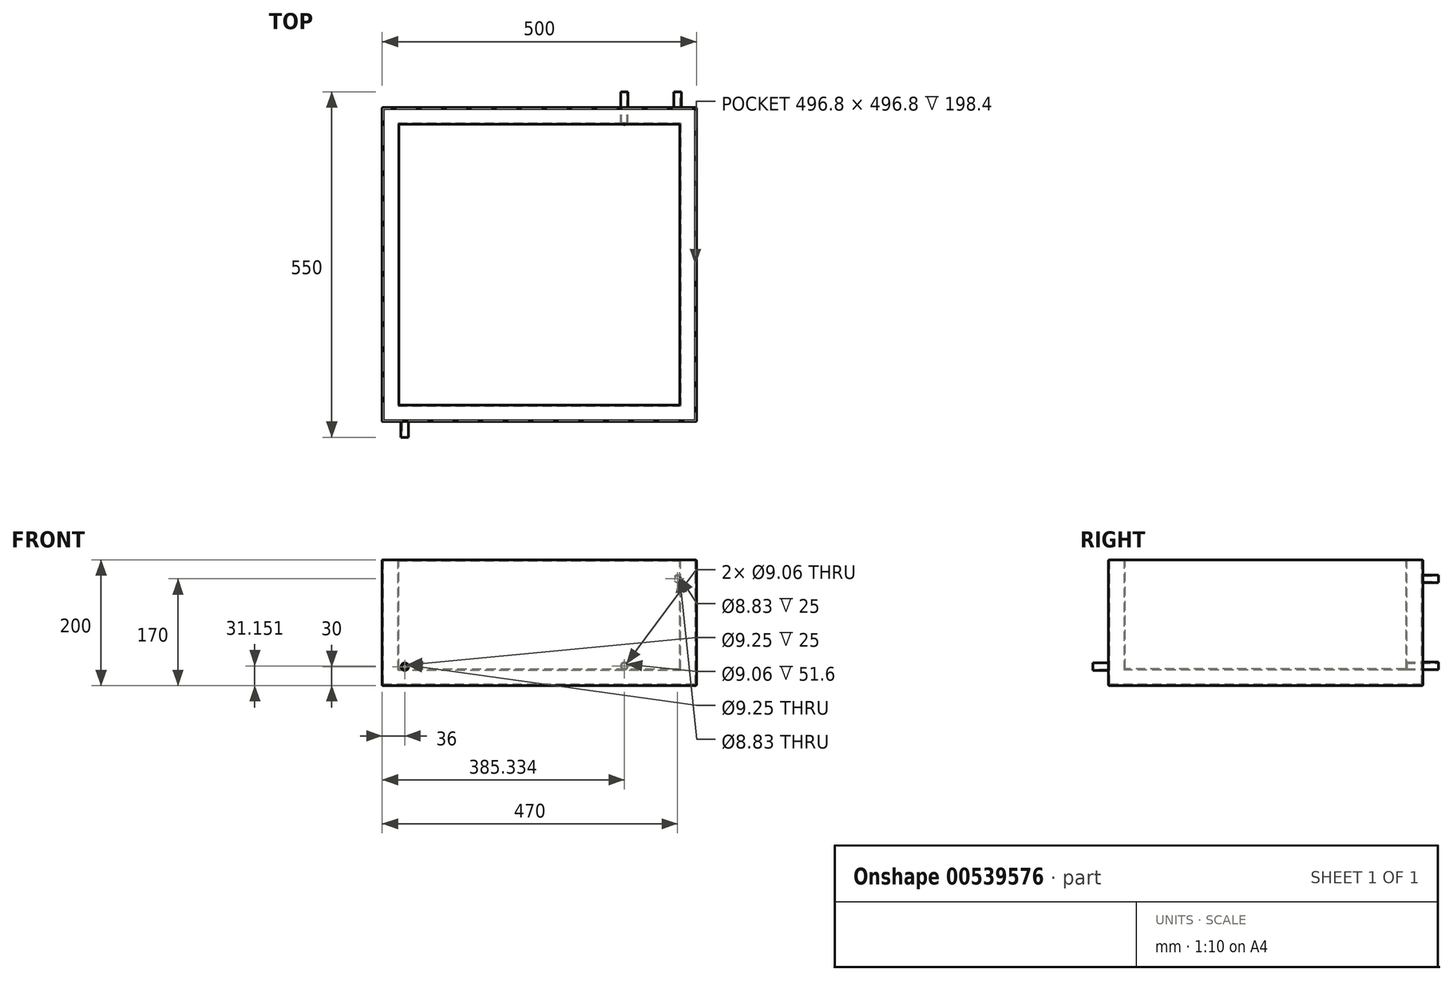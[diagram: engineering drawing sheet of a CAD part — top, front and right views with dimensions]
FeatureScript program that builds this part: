
annotation { "Feature Type Name" : "Feature", "Feature Type Description" : "" }
export const myFeature = defineFeature(function(context is Context, id is Id, definition is map)
    precondition{}
    {
        {
            var Q0;
            Q0=qCreatedBy(makeId("Top.planeOp"),FACE);
            var sketch = newSketch(context, id + "F0", { "sketchPlane" : qUnion([Q0])});
            skLineSegment(sketch, "E0.bottom", {"start": v(250, 250) * mm, "end": v(-250, 250) * mm});
            skLineSegment(sketch, "E0.top", {"start": v(250, -250) * mm, "end": v(-250, -250) * mm});
            skLineSegment(sketch, "E0.left", {"start": v(250, 250) * mm, "end": v(250, -250) * mm});
            skLineSegment(sketch, "E0.right", {"start": v(-250, 250) * mm, "end": v(-250, -250) * mm});
            skPoint(sketch, "E0.middle", {"position": v(0, 0) * mm});
            skSolve(sketch);
        }
        {
            var Q0;
            Q0 = qSketchRegion(id + "F0", true);
            extrude(context, id + "F1", {"entities" : qUnion([Q0]), "depth" : 200 * mm, "offsetDistance" : 25 * mm});
        }
        {
            var Q0;
            Q0=makeQuery(id+"F1.opExtrude","CAP_FACE",FACE,{"disambiguationData":[OSD([sQuery(id+"F0.wireOp",EDGE,"E0.bottom"),sQuery(id+"F0.wireOp",EDGE,"E0.top"),sQuery(id+"F0.wireOp",EDGE,"E0.left"),sQuery(id+"F0.wireOp",EDGE,"E0.right")])],"isStart":true});
            var Q1;
            Q1=makeQuery(id+"F1.opExtrude","SWEPT_EDGE",EDGE,{"disambiguationData":[OSD([sQuery(id+"F0.wireOp",EDGE,"E0.top"),sQuery(id+"F0.wireOp",EDGE,"E0.left")])]});
            var Q2;
            Q2=makeQuery(id+"F1.opExtrude","SWEPT_EDGE",EDGE,{"disambiguationData":[OSD([sQuery(id+"F0.wireOp",EDGE,"E0.top"),sQuery(id+"F0.wireOp",EDGE,"E0.right")])]});
            var Q3;
            Q3=makeQuery(id+"F1.opExtrude","SWEPT_EDGE",EDGE,{"disambiguationData":[OSD([sQuery(id+"F0.wireOp",EDGE,"E0.bottom"),sQuery(id+"F0.wireOp",EDGE,"E0.right")])]});
            var Q4;
            Q4=makeQuery(id+"F1.opExtrude","SWEPT_EDGE",EDGE,{"disambiguationData":[OSD([sQuery(id+"F0.wireOp",EDGE,"E0.bottom"),sQuery(id+"F0.wireOp",EDGE,"E0.left")])]});
            fillet(context, id + "F2", {"entities" : qUnion([Q0, Q1, Q2, Q3, Q4]), "radius" : 1 * mm, "tangentPropagation" : true, "allowEdgeOverflow" : false});
        }
        {
            var Q0;
            Q0=makeQuery(id+"F1.opExtrude","CAP_FACE",FACE,{"disambiguationData":[OSD([sQuery(id+"F0.wireOp",EDGE,"E0.bottom"),sQuery(id+"F0.wireOp",EDGE,"E0.top"),sQuery(id+"F0.wireOp",EDGE,"E0.left"),sQuery(id+"F0.wireOp",EDGE,"E0.right")])],"isStart":false});
            shell(context, id + "F3", {"entities" : qUnion([Q0]), "thickness" : 1.6 * mm});
        }
        {
            var Q0;
            Q0=makeQuery(id+"F1.opExtrude","CAP_FACE",FACE,{"disambiguationData":[OSD([sQuery(id+"F0.wireOp",EDGE,"E0.bottom"),sQuery(id+"F0.wireOp",EDGE,"E0.top"),sQuery(id+"F0.wireOp",EDGE,"E0.left"),sQuery(id+"F0.wireOp",EDGE,"E0.right")])],"isStart":false});
            var sketch = newSketch(context, id + "F4", { "sketchPlane" : qUnion([Q0])});
            skLineSegment(sketch, "E1.bottom", {"start": v(-225, 225) * mm, "end": v(225, 225) * mm});
            skLineSegment(sketch, "E1.top", {"start": v(-225, -225) * mm, "end": v(225, -225) * mm});
            skLineSegment(sketch, "E1.left", {"start": v(-225, 225) * mm, "end": v(-225, -225) * mm});
            skLineSegment(sketch, "E1.right", {"start": v(225, 225) * mm, "end": v(225, -225) * mm});
            skPoint(sketch, "E1.middle", {"position": v(0, 0) * mm});
            skLineSegment(sketch, "E2.bottom", {"start": v(-249, 249) * mm, "end": v(249, 249) * mm});
            skLineSegment(sketch, "E2.top", {"start": v(-249, -249) * mm, "end": v(249, -249) * mm});
            skLineSegment(sketch, "E2.left", {"start": v(-249, 249) * mm, "end": v(-249, -249) * mm});
            skLineSegment(sketch, "E2.right", {"start": v(249, 249) * mm, "end": v(249, -249) * mm});
            skSolve(sketch);
        }
        {
            var Q0;
            Q0=makeQuery(id+"F4.imprint","IMPRINT",FACE,{"disambiguationData":[TD([[makeQuery(id+"F4.imprint","IMPRINT",EDGE,{"derivedFrom":sQuery(id+"F4.wireOp",EDGE,"E1.bottom")}),1.0]])]});
            extrude(context, id + "F5", {"entities" : qUnion([Q0]), "oppositeDirection" : true, "depth" : 1.6 * mm, "offsetDistance" : 25 * mm});
        }
        {
            var Q0;
            Q0=makeQuery(id+"F5.opExtrude","CAP_FACE",FACE,{"disambiguationData":[OSD([sQuery(id+"F0.wireOp",EDGE,"E0.bottom"),sQuery(id+"F0.wireOp",EDGE,"E0.top"),sQuery(id+"F0.wireOp",EDGE,"E0.left"),sQuery(id+"F0.wireOp",EDGE,"E0.right"),sQuery(id+"F4.wireOp",EDGE,"E1.bottom"),sQuery(id+"F4.wireOp",EDGE,"E1.top"),sQuery(id+"F4.wireOp",EDGE,"E1.left"),sQuery(id+"F4.wireOp",EDGE,"E1.right")])],"isStart":true});
            var sketch = newSketch(context, id + "F6", { "sketchPlane" : qUnion([Q0])});
            skLineSegment(sketch, "E3.bottom", {"start": v(-225, -225) * mm, "end": v(225, -225) * mm});
            skLineSegment(sketch, "E3.top", {"start": v(-225, 225) * mm, "end": v(225, 225) * mm});
            skLineSegment(sketch, "E3.left", {"start": v(-225, -225) * mm, "end": v(-225, 225) * mm});
            skLineSegment(sketch, "E3.right", {"start": v(225, -225) * mm, "end": v(225, 225) * mm});
            skPoint(sketch, "E3.middle", {"position": v(0, 0) * mm});
            skSolve(sketch);
        }
        {
            var Q0;
            Q0 = qSketchRegion(id + "F6", true);
            extrude(context, id + "F7", {"entities" : qUnion([Q0]), "operationType" : NewBodyOperationType.ADD, "oppositeDirection" : true, "depth" : 175 * mm, "offsetDistance" : 25 * mm});
        }
        {
            var Q0;
            Q0=makeQuery(id+"F7.boolean.opBoolean","MERGE",FACE,{"derivedFrom":[makeQuery(id+"F5.opExtrude","CAP_FACE",FACE,{"disambiguationData":[OSD([sQuery(id+"F0.wireOp",EDGE,"E0.bottom"),sQuery(id+"F0.wireOp",EDGE,"E0.top"),sQuery(id+"F0.wireOp",EDGE,"E0.left"),sQuery(id+"F0.wireOp",EDGE,"E0.right"),sQuery(id+"F4.wireOp",EDGE,"E1.bottom"),sQuery(id+"F4.wireOp",EDGE,"E1.top"),sQuery(id+"F4.wireOp",EDGE,"E1.left"),sQuery(id+"F4.wireOp",EDGE,"E1.right")])],"isStart":true}),makeQuery(id+"F7.opExtrude","CAP_FACE",FACE,{"disambiguationData":[OSD([sQuery(id+"F6.wireOp",EDGE,"E3.bottom"),sQuery(id+"F6.wireOp",EDGE,"E3.top"),sQuery(id+"F6.wireOp",EDGE,"E3.left"),sQuery(id+"F6.wireOp",EDGE,"E3.right")])],"isStart":true})]});
            shell(context, id + "F8", {"entities" : qUnion([Q0]), "thickness" : 1.6 * mm});
        }
        {
            var Q0;
            Q0=makeQuery(id+"F8.opShell","OFFSET_EDGE",EDGE,{"disambiguationData":[OSD([sQuery(id+"F4.wireOp",EDGE,"E1.left")])]});
            var Q1;
            Q1=makeQuery(id+"F8.opShell","OFFSET_EDGE",EDGE,{"disambiguationData":[OSD([sQuery(id+"F4.wireOp",EDGE,"E1.top")])]});
            var Q2;
            Q2=makeQuery(id+"F8.opShell","OFFSET_EDGE",EDGE,{"disambiguationData":[OSD([sQuery(id+"F4.wireOp",EDGE,"E1.bottom")])]});
            var Q3;
            Q3=makeQuery(id+"F8.opShell","OFFSET_EDGE",EDGE,{"disambiguationData":[OSD([sQuery(id+"F4.wireOp",EDGE,"E1.right")])]});
            var Q4;
            Q4=makeQuery(id+"F8.opShell","OFFSET_EDGE",EDGE,{"disambiguationData":[OSD([sQuery(id+"F6.wireOp",EDGE,"E3.top"),sQuery(id+"F6.wireOp",EDGE,"E3.left")])]});
            var Q5;
            Q5=makeQuery(id+"F8.opShell","OFFSET_FACE",FACE,{"disambiguationData":[OSD([sQuery(id+"F6.wireOp",EDGE,"E3.bottom"),sQuery(id+"F6.wireOp",EDGE,"E3.top"),sQuery(id+"F6.wireOp",EDGE,"E3.left"),sQuery(id+"F6.wireOp",EDGE,"E3.right")])]});
            var Q6;
            Q6=makeQuery(id+"F8.opShell","OFFSET_EDGE",EDGE,{"disambiguationData":[OSD([sQuery(id+"F6.wireOp",EDGE,"E3.bottom"),sQuery(id+"F6.wireOp",EDGE,"E3.right")])]});
            var Q7;
            Q7=makeQuery(id+"F8.opShell","OFFSET_EDGE",EDGE,{"disambiguationData":[OSD([sQuery(id+"F6.wireOp",EDGE,"E3.bottom"),sQuery(id+"F6.wireOp",EDGE,"E3.left")])]});
            var Q8;
            Q8=makeQuery(id+"F8.opShell","OFFSET_EDGE",EDGE,{"disambiguationData":[OSD([sQuery(id+"F6.wireOp",EDGE,"E3.top"),sQuery(id+"F6.wireOp",EDGE,"E3.right")])]});
            var Q9;
            Q9=makeQuery(id+"F1.opExtrude","CAP_EDGE",EDGE,{"disambiguationData":[OSD([sQuery(id+"F0.wireOp",EDGE,"E0.right")])],"isStart":false});
            var Q10;
            Q10=makeQuery(id+"F1.opExtrude","CAP_EDGE",EDGE,{"disambiguationData":[OSD([sQuery(id+"F0.wireOp",EDGE,"E0.top")])],"isStart":false});
            var Q11;
            Q11=makeQuery(id+"F1.opExtrude","CAP_EDGE",EDGE,{"disambiguationData":[OSD([sQuery(id+"F0.wireOp",EDGE,"E0.left")])],"isStart":false});
            var Q12;
            Q12=makeQuery(id+"F1.opExtrude","CAP_EDGE",EDGE,{"disambiguationData":[OSD([sQuery(id+"F0.wireOp",EDGE,"E0.bottom")])],"isStart":false});
            fillet(context, id + "F9", {"entities" : qUnion([Q0, Q1, Q2, Q3, Q4, Q5, Q6, Q7, Q8, Q9, Q10, Q11, Q12]), "radius" : 1 * mm, "tangentPropagation" : true, "allowEdgeOverflow" : false});
        }
        {
            var Q0;
            Q0=makeQuery(id+"F1.opExtrude","SWEPT_FACE",FACE,{"disambiguationData":[OSD([sQuery(id+"F0.wireOp",EDGE,"E0.bottom")])]});
            var sketch = newSketch(context, id + "F10", { "sketchPlane" : qUnion([Q0])});
            skCircle(sketch, "E4", {"center": v(-220, 170) * mm, "radius": 6 * mm});
            skSolve(sketch);
        }
        {
            var Q0;
            Q0 = qSketchRegion(id + "F10", true);
            var Q1;
            Q1=sQuery(id+"F10.wireOp",EDGE,"E4");
            extrude(context, id + "F11", {"entities" : qUnion([Q0]), "surfaceEntities" : qUnion([Q1]), "depth" : 25 * mm, "offsetDistance" : 25 * mm});
        }
        {
            var Q0;
            Q0=makeQuery(id+"F1.opExtrude","SWEPT_FACE",FACE,{"disambiguationData":[OSD([sQuery(id+"F0.wireOp",EDGE,"E0.top")])]});
            var sketch = newSketch(context, id + "F12", { "sketchPlane" : qUnion([Q0])});
            skCircle(sketch, "E5", {"center": v(-214, 30) * mm, "radius": 6 * mm});
            skSolve(sketch);
        }
        {
            var Q0;
            Q0 = qSketchRegion(id + "F12", true);
            var Q1;
            Q1=sQuery(id+"F12.wireOp",EDGE,"E5");
            extrude(context, id + "F13", {"entities" : qUnion([Q0]), "surfaceEntities" : qUnion([Q1]), "depth" : 25 * mm, "offsetDistance" : 25 * mm});
        }
        {
            var Q0;
            Q0=makeQuery(id+"F13.opExtrude","CAP_FACE",FACE,{"disambiguationData":[OSD([sQuery(id+"F12.wireOp",EDGE,"E5")])],"isStart":false});
            var sketch = newSketch(context, id + "F14", { "sketchPlane" : qUnion([Q0])});
            skCircle(sketch, "E6", {"center": v(-214, 30) * mm, "radius": 4.63 * mm});
            skSolve(sketch);
        }
        {
            var Q0;
            Q0 = qSketchRegion(id + "F14", true);
            extrude(context, id + "F15", {"entities" : qUnion([Q0]), "operationType" : NewBodyOperationType.REMOVE, "oppositeDirection" : true, "depth" : 30 * mm, "offsetDistance" : 25 * mm});
        }
        {
            var Q0;
            Q0=makeQuery(id+"F11.opExtrude","CAP_FACE",FACE,{"disambiguationData":[OSD([sQuery(id+"F10.wireOp",EDGE,"E4")])],"isStart":false});
            var sketch = newSketch(context, id + "F16", { "sketchPlane" : qUnion([Q0])});
            skCircle(sketch, "E7", {"center": v(-220, 170) * mm, "radius": 4.42 * mm});
            skSolve(sketch);
        }
        {
            var Q0;
            Q0 = qSketchRegion(id + "F16", true);
            extrude(context, id + "F17", {"entities" : qUnion([Q0]), "operationType" : NewBodyOperationType.REMOVE, "oppositeDirection" : true, "depth" : 30 * mm, "offsetDistance" : 25 * mm});
        }
        {
            var Q0;
            Q0=makeQuery(id+"F1.opExtrude","SWEPT_FACE",FACE,{"disambiguationData":[OSD([sQuery(id+"F0.wireOp",EDGE,"E0.bottom")])]});
            var sketch = newSketch(context, id + "F18", { "sketchPlane" : qUnion([Q0])});
            skCircle(sketch, "E8", {"center": v(-135.33, 31.15) * mm, "radius": 6 * mm});
            skSolve(sketch);
        }
        {
            var Q0;
            Q0 = qSketchRegion(id + "F18", true);
            var Q1;
            Q1=makeQuery(id+"F8.opShell","OFFSET_FACE",FACE,{"disambiguationData":[OSD([sQuery(id+"F6.wireOp",EDGE,"E3.top")])]});
            extrude(context, id + "F19", {"entities" : qUnion([Q0]), "endBound" : BoundingType.UP_TO_SURFACE, "oppositeDirection" : true, "depth" : 25 * mm, "endBoundEntityFace" : qUnion([Q1]), "offsetDistance" : 25 * mm, "hasSecondDirection" : true, "secondDirectionOppositeDirection" : false, "secondDirectionDepth" : 25 * mm});
        }
        {
            var Q0;
            Q0=makeQuery(id+"F19.opExtrude","CAP_FACE",FACE,{"disambiguationData":[OSD([sQuery(id+"F18.wireOp",EDGE,"E8")])],"isStart":true});
            var sketch = newSketch(context, id + "F20", { "sketchPlane" : qUnion([Q0])});
            skCircle(sketch, "E9", {"center": v(-135.33, 31.15) * mm, "radius": 4.53 * mm});
            skSolve(sketch);
        }
        {
            var Q0;
            Q0 = qSketchRegion(id + "F20", true);
            extrude(context, id + "F21", {"entities" : qUnion([Q0]), "operationType" : NewBodyOperationType.REMOVE, "oppositeDirection" : true, "depth" : 70 * mm, "offsetDistance" : 25 * mm});
        }
    });
